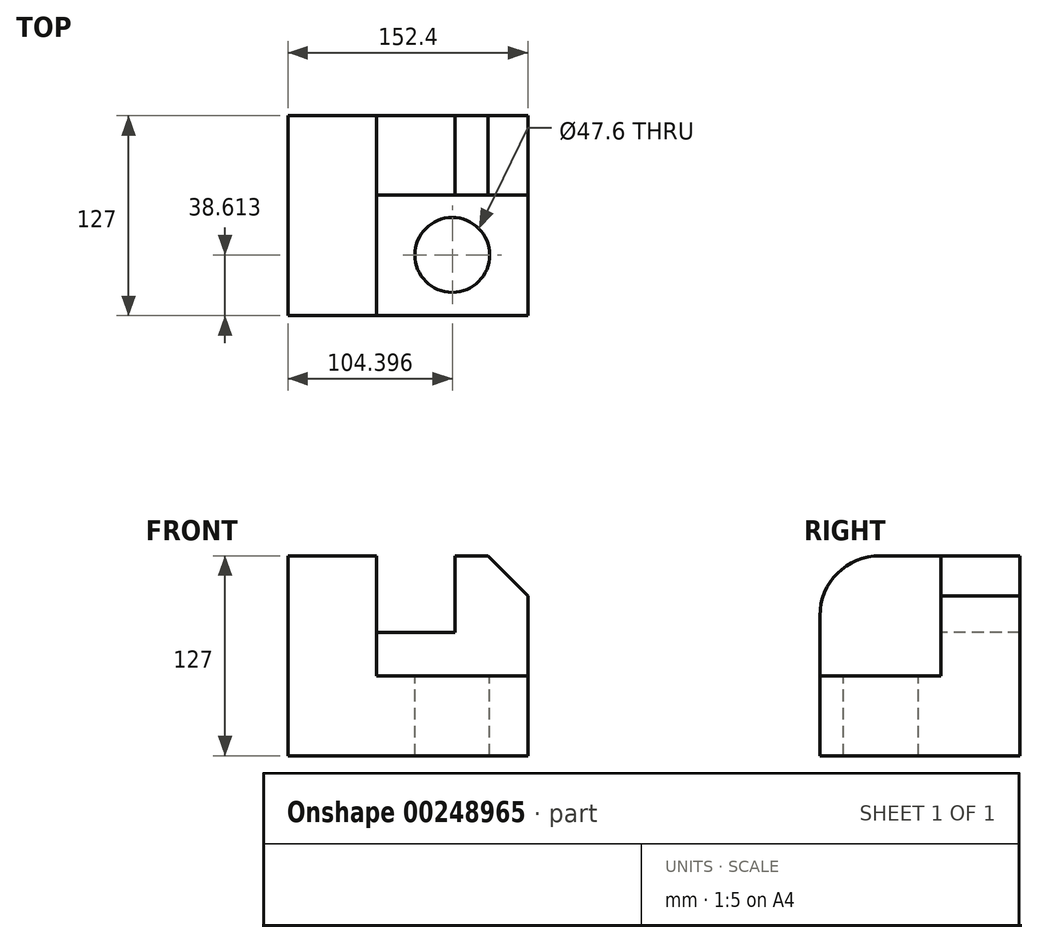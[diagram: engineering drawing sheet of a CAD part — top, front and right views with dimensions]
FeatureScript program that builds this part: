
annotation { "Feature Type Name" : "Feature", "Feature Type Description" : "" }
export const myFeature = defineFeature(function(context is Context, id is Id, definition is map)
    precondition{}
    {
        {
            var Q0;
            Q0=qCreatedBy(makeId("Front.planeOp"),FACE);
            var sketch = newSketch(context, id + "F0", { "sketchPlane" : qUnion([Q0])});
            skLineSegment(sketch, "E0.bottom", {"start": v(-76.2, 63.5) * mm, "end": v(76.2, 63.5) * mm});
            skLineSegment(sketch, "E0.top", {"start": v(-76.2, -63.5) * mm, "end": v(76.2, -63.5) * mm});
            skLineSegment(sketch, "E0.left", {"start": v(-76.2, 63.5) * mm, "end": v(-76.2, -63.5) * mm});
            skLineSegment(sketch, "E0.right", {"start": v(76.2, 63.5) * mm, "end": v(76.2, -63.5) * mm});
            skPoint(sketch, "E0.middle", {"position": v(0, 0) * mm});
            skSolve(sketch);
        }
        {
            var Q0;
            Q0 = qSketchRegion(id + "F0", true);
            extrude(context, id + "F1", {"entities" : qUnion([Q0]), "endBound" : BoundingType.SYMMETRIC, "depth" : 127 * mm});
        }
        {
            var Q0;
            Q0=makeQuery(id+"F1.opExtrude","SWEPT_FACE",FACE,{"disambiguationData":[OSD([sQuery(id+"F0.wireOp",EDGE,"E0.bottom")])]});
            var sketch = newSketch(context, id + "F2", { "sketchPlane" : qUnion([Q0])});
            skLineSegment(sketch, "E1", {"start": v(-76.2, -63.5) * mm, "end": v(-19.8, -63.5) * mm});
            skLineSegment(sketch, "E2", {"start": v(-19.8, -63.5) * mm, "end": v(-19.8, 13.2) * mm});
            skLineSegment(sketch, "E3", {"start": v(-19.8, 13.2) * mm, "end": v(76.2, 13.2) * mm});
            skLineSegment(sketch, "E4", {"start": v(76.2, 13.2) * mm, "end": v(76.2, 63.5) * mm});
            skLineSegment(sketch, "E5", {"start": v(76.2, 63.5) * mm, "end": v(-76.2, 63.5) * mm});
            skLineSegment(sketch, "E6", {"start": v(-76.2, 63.5) * mm, "end": v(-76.2, -63.5) * mm});
            skSolve(sketch);
        }
        {
            var Q0;
            {var subQ0=sQuery(id+"F2.wireOp",EDGE,"E2");Q0=makeQuery(id+"F2.imprint","IMPRINT",FACE,{"disambiguationData":[TD([[makeQuery(id+"F2.imprint","IMPRINT",EDGE,{"derivedFrom":subQ0}),-1.0]])]});}
            extrude(context, id + "F3", {"entities" : qUnion([Q0]), "operationType" : NewBodyOperationType.REMOVE, "oppositeDirection" : true, "depth" : 76.2 * mm});
        }
        {
            var Q0;
            Q0=makeQuery(id+"F3.boolean.opBoolean","COPY",FACE,{"derivedFrom":makeQuery(id+"F3.opExtrude","SWEPT_FACE",FACE,{"disambiguationData":[OSD([sQuery(id+"F2.wireOp",EDGE,"E3")])]})});
            var sketch = newSketch(context, id + "F4", { "sketchPlane" : qUnion([Q0])});
            skLineSegment(sketch, "E7.bottom", {"start": v(-19.8, 63.5) * mm, "end": v(29.84, 63.5) * mm});
            skLineSegment(sketch, "E7.top", {"start": v(-19.8, 14.97) * mm, "end": v(29.84, 14.97) * mm});
            skLineSegment(sketch, "E7.left", {"start": v(-19.8, 63.5) * mm, "end": v(-19.8, 14.97) * mm});
            skLineSegment(sketch, "E7.right", {"start": v(29.84, 63.5) * mm, "end": v(29.84, 14.97) * mm});
            skSolve(sketch);
        }
        {
            var Q0;
            Q0=makeQuery(id+"F4.imprint","IMPRINT",FACE,{"disambiguationData":[TD([[makeQuery(id+"F4.imprint","IMPRINT",EDGE,{"derivedFrom":sQuery(id+"F4.wireOp",EDGE,"E7.bottom")}),-1.0]])]});
            extrude(context, id + "F5", {"entities" : qUnion([Q0]), "operationType" : NewBodyOperationType.REMOVE, "oppositeDirection" : true, "depth" : 75.18 * mm});
        }
        {
            var Q0;
            Q0=makeQuery(id+"F1.opExtrude","CAP_EDGE",EDGE,{"disambiguationData":[OSD([sQuery(id+"F0.wireOp",EDGE,"E0.bottom")])],"isStart":false});
            fillet(context, id + "F6", {"entities" : qUnion([Q0]), "radius" : 38.1 * mm, "tangentPropagation" : true, "allowEdgeOverflow" : false});
        }
        {
            var Q0;
            Q0=makeQuery(id+"F1.opExtrude","SWEPT_EDGE",EDGE,{"disambiguationData":[OSD([sQuery(id+"F0.wireOp",EDGE,"E0.bottom"),sQuery(id+"F0.wireOp",EDGE,"E0.right")])]});
            chamfer(context, id + "F7", {"entities" : qUnion([Q0]), "width" : 25.4 * mm, "tangentPropagation" : true});
        }
        {
            var Q0;
            Q0=makeQuery(id+"F3.boolean.opBoolean","COPY",FACE,{"derivedFrom":makeQuery(id+"F3.opExtrude","CAP_FACE",FACE,{"disambiguationData":[OSD([sQuery(id+"F0.wireOp",EDGE,"E0.bottom"),sQuery(id+"F0.wireOp",EDGE,"E0.right"),sQuery(id+"F2.wireOp",EDGE,"E2"),sQuery(id+"F2.wireOp",EDGE,"E3")])],"isStart":false})});
            var sketch = newSketch(context, id + "F8", { "sketchPlane" : qUnion([Q0])});
            skCircle(sketch, "E8", {"center": v(28.2, -24.89) * mm, "radius": 23.8 * mm});
            skSolve(sketch);
        }
        {
            var Q0;
            Q0=makeQuery(id+"F8.imprint","IMPRINT",FACE,{"disambiguationData":[TD([[makeQuery(id+"F8.imprint","IMPRINT",EDGE,{"derivedFrom":sQuery(id+"F8.wireOp",EDGE,"E8")}),1.0]])]});
            extrude(context, id + "F9", {"entities" : qUnion([Q0]), "operationType" : NewBodyOperationType.REMOVE, "oppositeDirection" : true, "depth" : 86.36 * mm});
        }
    });
